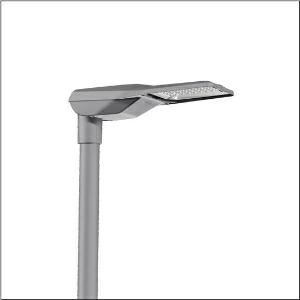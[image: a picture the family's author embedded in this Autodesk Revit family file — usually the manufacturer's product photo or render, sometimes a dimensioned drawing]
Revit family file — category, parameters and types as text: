
# Revit family: streetlight_sl_21_iq_mini___stw1_0a_5xe2e41g08hb_6f26
name_source: partatom
category: Lighting Fixtures
units: mm (PartAtom-declared; Revit-internal decimal feet)

## family parameters
Cut with Voids When Loaded = No
Host = Face
Light Source = No
Part Type = Normal
Room Calculation Point = No
Round Connector Dimension = Use Diameter
Shared = No

## types (1)
- --- (1 x LED, 9860 lm, 70.9 W, 4000K)
    Apparent Load = 71 VA
    CIE Flux Codes = 38 75 98 100 100
    Color Rendering = 70
    Color Temperature = 4000K
    Default Elevation = 1800 mm
    Description = Streetlight SL 21 iQ mini, mast luminaire, primary light control with lens, of PMMA, primary optical cover: cover, of toughened safety glass, transparent, light distribution: STW1.0a, light emission: direct distribution, primary light characteristic: asymmetric, installation type: post-top, side-entry, LED, High Power LED, rated luminous flux: 9.860lm, luminous efficacy: 139lm/W, light colour: 740, colour temperature: 4000K, control: Street-Remote, Auto-Match, Temp-Guard, Lumen-Switch, Night-Set, Smart-Wire, Light-Fading, Desk-Remote (wireless, voltage-free reading and setting of iQ features in the workshop via application-optimized NFC function/RFID function), optimised constant luminous flux control (CLO 2.0), pre-setting: linear dimming characteristic, mains connection: 220..240V, AC, 50/60Hz, start of lifetime: 71W, end of service life: 75W, reduction: 31W, luminaire housing, of diecast aluminium, powder-coated, Siteco® metallic grey (DB 702S), corrosivity category C5 mid according to DIN EN ISO 12944, please order mast flange separately, inclination adjustable: 0°, 5°, 10°, 15°, sealing non-destructively replaceable, multi-level sealing system, length: 628mm, width: 235mm, height: 110mm, mast flange for spigot size: 42mm (side-entry): 5XC10008XM4, 60/48mm (side-entry/post-top): 5XC10108XM2, 76/60mm (side-entry/post-top): 5XC10108XM1, protection rating (complete): IP66, insulation class (complete): insulation class II (safety insulation), certification: CE, ENEC, ENEC+, VDE, impact resistance: IK09, permissible operating ambient temperature for outdoor applications: -40..+50°C, standard-compliant lighting for roads and squares, packaging unit: 1 piece

Light Distribution: STW1.0a
    Height = 110 mm
    Lamp = 1 x LED
    Lamp Light Flux = 9860 lm
    Lamp Power = 70.9 W
    Lamp count = 1
    Length = 625 mm
    Luminous efficacy = 139 lm/W
    Manufacturer = Siteco
    ModVariant = No
    Model = 5XE2E41G08HB
    Number of Poles = 1
    OnlyDefault = Yes
    Power Factor = 1
    Product Name = Streetlight SL 21 iQ mini | STW1.0a
    Product group = mast luminaire | pylon top
    ProductGroupID = 6100
    Protection Class = Protection class II
    Protection Degree = IP 66
    RLX_Detail_Level = 1
    RLX_Emergency_Light_Flux = 0 lm
    RLX_Emergency_Type = 0
    RLX_Emergency_Type_DB = No
    RlxData = <blob elided: 92441 chars, md5=6e4b14a1>
    Socket = socket
    Standby Power = 0 W
    System Light Flux = 9860 lm
    System Power = 71 W
    Type Comments = factory setting: luminous flux: 100 % | dim-lin: 254 | 711 mA
    Type Image = l_1003519.jpg
    URL = http://relux.com
    VarID = @adj_128103
    Voltage = 0 V
    Weight = 0.00 kg
    Width = 234 mm

## geometry (parser evidence)
native form markers: Blend x4, Sweep x11
no freeform markers — native parametric forms only
